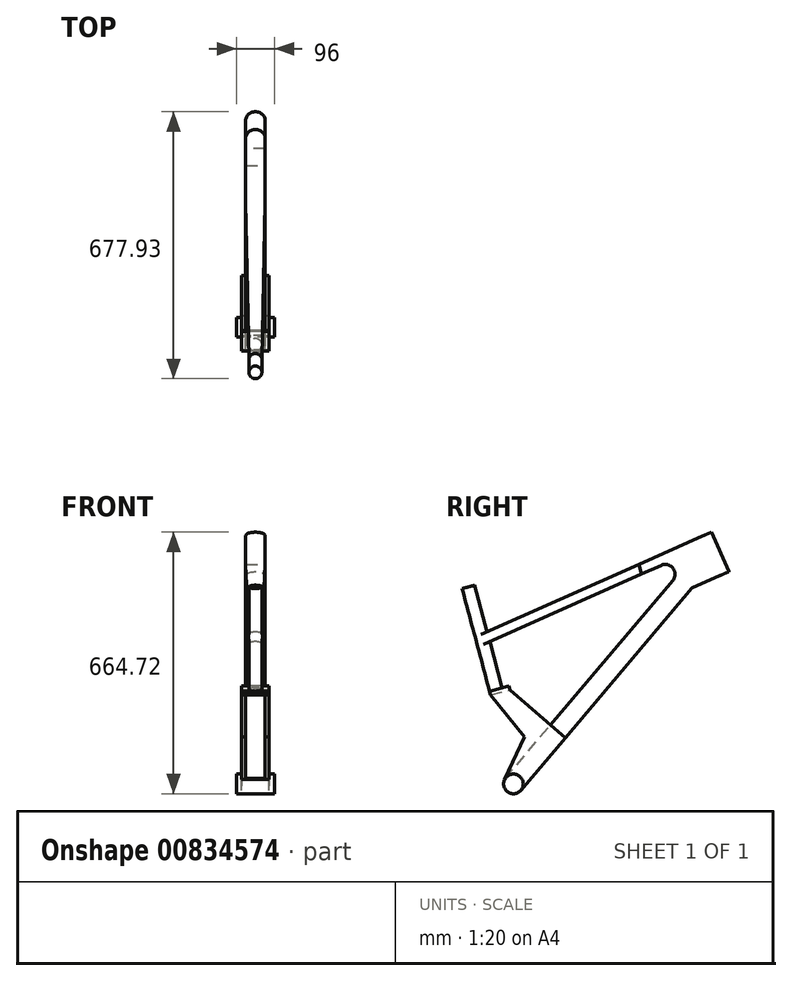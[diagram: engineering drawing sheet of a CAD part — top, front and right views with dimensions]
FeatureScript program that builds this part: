
annotation { "Feature Type Name" : "Feature", "Feature Type Description" : "" }
export const myFeature = defineFeature(function(context is Context, id is Id, definition is map)
    precondition{}
    {
        {
            var Q0;
            Q0=qCreatedBy(makeId("Right.planeOp"),FACE);
            var sketch = newSketch(context, id + "F0", { "sketchPlane" : qUnion([Q0])});
            skLineSegment(sketch, "E0", {"start": v(15, 17.71) * mm, "end": v(-114.4, 500.68) * mm});
            skCircle(sketch, "E1", {"center": v(0, 0) * mm, "radius": 25 * mm});
            skLineSegment(sketch, "E2", {"start": v(0, 0) * mm, "end": v(0, 629.55) * mm});
            skLineSegment(sketch, "E3", {"start": v(0, 629.55) * mm, "end": v(480, 629.55) * mm});
            skLineSegment(sketch, "E4", {"start": v(480, 629.55) * mm, "end": v(524.74, 529.06) * mm});
            skLineSegment(sketch, "E5", {"start": v(-148.94, 629.55) * mm, "end": v(480, 629.55) * mm});
            skLineSegment(sketch, "E6", {"start": v(0, 0) * mm, "end": v(991.3, 0) * mm});
            skLineSegment(sketch, "E7", {"start": v(524.74, 529.06) * mm, "end": v(571.33, 549.8) * mm});
            skLineSegment(sketch, "E8", {"start": v(571.33, 549.8) * mm, "end": v(802.76, 30) * mm});
            skCircle(sketch, "E9", {"center": v(802.76, 30) * mm, "radius": 368.5 * mm});
            skLineSegment(sketch, "E10", {"start": v(-560.19, -338.5) * mm, "end": v(1095.06, -338.5) * mm});
            skLineSegment(sketch, "E11", {"start": v(480, 629.55) * mm, "end": v(-81.9, 379.38) * mm});
            skCircle(sketch, "E12", {"center": v(-435, 30) * mm, "radius": 368.5 * mm});
            skLineSegment(sketch, "E13", {"start": v(0, 0) * mm, "end": v(498.3, 588.44) * mm});
            skLineSegment(sketch, "E14", {"start": v(0, 0) * mm, "end": v(-435, 0) * mm});
            skLineSegment(sketch, "E15", {"start": v(-114.4, 500.68) * mm, "end": v(-148.94, 629.55) * mm});
            skSolve(sketch);
        }
        {
            var Q0;
            Q0=qCreatedBy(makeId("Right.planeOp"),FACE);
            var sketch = newSketch(context, id + "F1", { "sketchPlane" : qUnion([Q0])});
            skLineSegment(sketch, "E16", {"start": v(480, 629.55) * mm, "end": v(502.84, 639.72) * mm});
            skLineSegment(sketch, "E17", {"start": v(524.74, 529.06) * mm, "end": v(547.58, 539.23) * mm});
            skLineSegment(sketch, "E18", {"start": v(480, 629.55) * mm, "end": v(524.74, 529.06) * mm});
            skLineSegment(sketch, "E19", {"start": v(502.84, 639.72) * mm, "end": v(547.58, 539.23) * mm});
            skSolve(sketch);
        }
        {
            var Q0;
            Q0=makeQuery(id+"F1.imprint","IMPRINT",FACE,{"disambiguationData":[TD([[makeQuery(id+"F1.imprint","IMPRINT",EDGE,{"derivedFrom":sQuery(id+"F1.wireOp",EDGE,"E16")}),-1.0]])]});
            var Q1;
            Q1=sQuery(id+"F1.wireOp",EDGE,"E18");
            revolve(context, id + "F2", {"surfaceOperationType" : NewSurfaceOperationType.NEW, "entities" : qUnion([Q0]), "axis" : qUnion([Q1]), "revolveType" : RevolveType.FULL, "oppositeDirection" : true});
        }
        {
            var Q0;
            Q0=sQuery(id+"F0.wireOp",EDGE,"E11");
            var Q1;
            Q1=sQuery(id+"F0.wireOp",VERTEX,"E3.end");
            cPlane(context, id + "F3", {"entities" : qUnion([Q0, Q1]), "cplaneType" : CPlaneType.LINE_POINT, "offset" : 25 * mm, "width" : 150 * mm, "height" : 150 * mm});
        }
        {
            var Q0;
            Q0=qCreatedBy(id+"F3.planeOp",FACE);
            var sketch = newSketch(context, id + "F4", { "sketchPlane" : qUnion([Q0])});
            skLineSegment(sketch, "E20.bottom", {"start": v(-25, 379.9) * mm, "end": v(25, 379.9) * mm});
            skLineSegment(sketch, "E20.top", {"start": v(-25, 354.9) * mm, "end": v(25, 354.9) * mm});
            skLineSegment(sketch, "E20.left", {"start": v(-25, 379.9) * mm, "end": v(-25, 354.9) * mm});
            skLineSegment(sketch, "E20.right", {"start": v(25, 379.9) * mm, "end": v(25, 354.9) * mm});
            skPoint(sketch, "E20.middle", {"position": v(0, 367.4) * mm});
            skPoint(sketch, "E21.visualSharp", {"position": v(25, 379.9) * mm});
            skPoint(sketch, "E22.visualSharp", {"position": v(25, 354.9) * mm});
            skPoint(sketch, "E23.visualSharp", {"position": v(-25, 354.9) * mm});
            skPoint(sketch, "E24.visualSharp", {"position": v(-25, 379.9) * mm});
            skSolve(sketch);
        }
        {
            var Q0;
            {var subQ0=sQuery(id+"F0.wireOp",EDGE,"E2");var subQ1=sQuery(id+"F0.wireOp",EDGE,"E1");var subQ2=makeQuery(id+"F0.imprint","INTERSECT",VERTEX,{"derivedFrom":[subQ1,subQ0]});Q0=makeQuery(id+"F0.imprint","IMPRINT",FACE,{"disambiguationData":[TD([[makeQuery(id+"F0.imprint","IMPRINT",EDGE,{"disambiguationData":[TD([[subQ2,-1.0]])],"derivedFrom":subQ1}),1.0]])]});}
            var Q1;
            {var subQ0=sQuery(id+"F0.wireOp",EDGE,"E1");var subQ1=sQuery(id+"F0.wireOp",EDGE,"E0");var subQ2=makeQuery(id+"F0.imprint","INTERSECT",VERTEX,{"derivedFrom":[subQ1,subQ0]});Q1=makeQuery(id+"F0.imprint","IMPRINT",FACE,{"disambiguationData":[TD([[makeQuery(id+"F0.imprint","IMPRINT",EDGE,{"disambiguationData":[TD([[subQ2,1.0]])],"derivedFrom":subQ1}),1.0]])]});}
            var Q2;
            {var subQ0=sQuery(id+"F0.wireOp",EDGE,"E1");var subQ1=sQuery(id+"F0.wireOp",EDGE,"E0");var subQ2=makeQuery(id+"F0.imprint","INTERSECT",VERTEX,{"derivedFrom":[subQ1,subQ0]});Q2=makeQuery(id+"F0.imprint","IMPRINT",FACE,{"disambiguationData":[TD([[makeQuery(id+"F0.imprint","IMPRINT",EDGE,{"disambiguationData":[TD([[subQ2,1.0]])],"derivedFrom":subQ1}),-1.0]])]});}
            var Q3;
            {var subQ0=sQuery(id+"F0.wireOp",EDGE,"E6");var subQ1=sQuery(id+"F0.wireOp",EDGE,"E1");var subQ2=makeQuery(id+"F0.imprint","INTERSECT",VERTEX,{"derivedFrom":[subQ1,subQ0]});Q3=makeQuery(id+"F0.imprint","IMPRINT",FACE,{"disambiguationData":[TD([[makeQuery(id+"F0.imprint","IMPRINT",EDGE,{"disambiguationData":[TD([[subQ2,-1.0]])],"derivedFrom":subQ1}),1.0]])]});}
            var Q4;
            {var subQ0=sQuery(id+"F0.wireOp",EDGE,"E6");var subQ1=sQuery(id+"F0.wireOp",EDGE,"E1");var subQ2=makeQuery(id+"F0.imprint","INTERSECT",VERTEX,{"derivedFrom":[subQ1,subQ0]});Q4=makeQuery(id+"F0.imprint","IMPRINT",FACE,{"disambiguationData":[TD([[makeQuery(id+"F0.imprint","IMPRINT",EDGE,{"disambiguationData":[TD([[subQ2,1.0]])],"derivedFrom":subQ1}),1.0]])]});}
            extrude(context, id + "F5", {"entities" : qUnion([Q0, Q1, Q2, Q3, Q4]), "endBound" : BoundingType.SYMMETRIC, "depth" : 96 * mm, "offsetDistance" : 25 * mm});
        }
        {
            var Q0;
            Q0=sQuery(id+"F0.wireOp",EDGE,"E13");
            var Q1;
            Q1=sQuery(id+"F0.wireOp",VERTEX,"E2.start");
            cPlane(context, id + "F6", {"entities" : qUnion([Q0, Q1]), "cplaneType" : CPlaneType.LINE_POINT, "offset" : 25 * mm, "width" : 150 * mm, "height" : 150 * mm});
        }
        {
            var Q0;
            Q0=qCreatedBy(id+"F6.planeOp",FACE);
            var sketch = newSketch(context, id + "F7", { "sketchPlane" : qUnion([Q0])});
            skLineSegment(sketch, "E25.bottom", {"start": v(25, -25) * mm, "end": v(-25, -25) * mm});
            skLineSegment(sketch, "E25.top", {"start": v(25, 25) * mm, "end": v(-25, 25) * mm});
            skPoint(sketch, "E25.middle", {"position": v(0, 0) * mm});
            skLineSegment(sketch, "E26", {"start": v(25, -25) * mm, "end": v(25, 25) * mm});
            skLineSegment(sketch, "E27", {"start": v(-25, -25) * mm, "end": v(-25, 25) * mm});
            skSolve(sketch);
        }
        {
            var Q0;
            Q0 = qSketchRegion(id + "F7", true);
            var Q1;
            Q1=makeQuery(id+"F2.opRevolve","SWEPT_FACE",FACE,{"disambiguationData":[OSD([sQuery(id+"F1.wireOp",EDGE,"E19")])]});
            extrude(context, id + "F8", {"entities" : qUnion([Q0]), "operationType" : NewBodyOperationType.ADD, "endBound" : BoundingType.UP_TO_SURFACE, "depth" : 25 * mm, "endBoundEntityFace" : qUnion([Q1]), "offsetDistance" : 25 * mm});
        }
        {
            var Q0;
            Q0=sQuery(id+"F0.wireOp",VERTEX,"E0.end");
            var Q1;
            Q1=sQuery(id+"F0.wireOp",EDGE,"E0");
            cPlane(context, id + "F9", {"entities" : qUnion([Q0, Q1]), "cplaneType" : CPlaneType.LINE_POINT, "offset" : 25 * mm, "width" : 150 * mm, "height" : 150 * mm});
        }
        {
            var Q0;
            Q0=qCreatedBy(id+"F9.planeOp",FACE);
            var sketch = newSketch(context, id + "F10", { "sketchPlane" : qUnion([Q0])});
            skCircle(sketch, "E28", {"center": v(0, 19.07) * mm, "radius": 16.5 * mm});
            skSolve(sketch);
        }
        {
            var Q0;
            Q0 = qSketchRegion(id + "F10", true);
            extrude(context, id + "F11", {"entities" : qUnion([Q0]), "oppositeDirection" : true, "depth" : 280 * mm, "offsetDistance" : 25 * mm});
        }
        {
            var Q0;
            Q0 = qSketchRegion(id + "F4", true);
            extrude(context, id + "F12", {"entities" : qUnion([Q0]), "operationType" : NewBodyOperationType.ADD, "depth" : 621 * mm, "offsetDistance" : 25 * mm});
        }
        {
            var Q0;
            Q0=makeQuery(id+"F12.boolean.opBoolean","MERGE",FACE,{"derivedFrom":[makeQuery(id+"F8.opExtrude","SWEPT_FACE",FACE,{"disambiguationData":[OSD([sQuery(id+"F7.wireOp",EDGE,"E26")])]}),makeQuery(id+"F12.opExtrude","SWEPT_FACE",FACE,{"disambiguationData":[OSD([sQuery(id+"F4.wireOp",EDGE,"E20.right")])]})]});
            var sketch = newSketch(context, id + "F13", { "sketchPlane" : qUnion([Q0])});
            skLineSegment(sketch, "E29", {"start": v(480, 629.55) * mm, "end": v(524.74, 529.06) * mm});
            skLineSegment(sketch, "E30", {"start": v(524.74, 529.06) * mm, "end": v(349, 450.82) * mm});
            skLineSegment(sketch, "E31", {"start": v(454.17, 497.64) * mm, "end": v(509.6, 563.09) * mm});
            skLineSegment(sketch, "E32", {"start": v(480, 629.55) * mm, "end": v(349, 571.23) * mm});
            skLineSegment(sketch, "E33", {"start": v(349, 571.23) * mm, "end": v(349, 450.82) * mm});
            skSolve(sketch);
        }
        {
            var Q0;
            Q0 = qSketchRegion(id + "F13", true);
            var Q1;
            Q1=makeQuery(id+"F12.boolean.opBoolean","MERGE",FACE,{"derivedFrom":[makeQuery(id+"F8.opExtrude","SWEPT_FACE",FACE,{"disambiguationData":[OSD([sQuery(id+"F7.wireOp",EDGE,"E27")])]}),makeQuery(id+"F12.opExtrude","SWEPT_FACE",FACE,{"disambiguationData":[OSD([sQuery(id+"F4.wireOp",EDGE,"E20.left")])]})]});
            extrude(context, id + "F14", {"entities" : qUnion([Q0]), "operationType" : NewBodyOperationType.ADD, "endBound" : BoundingType.UP_TO_SURFACE, "oppositeDirection" : true, "depth" : 25 * mm, "endBoundEntityFace" : qUnion([Q1]), "offsetDistance" : 25 * mm});
        }
        {
            var Q0;
            Q0=makeQuery(id+"F14.boolean.opBoolean","MERGE",FACE,{"derivedFrom":[makeQuery(id+"F12.boolean.opBoolean","MERGE",FACE,{"derivedFrom":[makeQuery(id+"F8.opExtrude","SWEPT_FACE",FACE,{"disambiguationData":[OSD([sQuery(id+"F7.wireOp",EDGE,"E26")])]}),makeQuery(id+"F12.opExtrude","SWEPT_FACE",FACE,{"disambiguationData":[OSD([sQuery(id+"F4.wireOp",EDGE,"E20.right")])]})]}),makeQuery(id+"F14.opExtrude","CAP_FACE",FACE,{"disambiguationData":[OSD([sQuery(id+"F13.wireOp",EDGE,"E29"),sQuery(id+"F13.wireOp",EDGE,"E30"),sQuery(id+"F13.wireOp",EDGE,"E32"),sQuery(id+"F13.wireOp",EDGE,"E33")])],"isStart":true})]});
            var sketch = newSketch(context, id + "F15", { "sketchPlane" : qUnion([Q0])});
            skLineSegment(sketch, "E34", {"start": v(349, 543.86) * mm, "end": v(375.52, 555.67) * mm});
            skLineSegment(sketch, "E35", {"start": v(349, 450.82) * mm, "end": v(404.77, 516.68) * mm});
            skArc(sketch, "E36", {"start": v(404.77, 516.68) * mm, "mid": v(405.7, 547.83) * mm, "end": v(375.52, 555.67) * mm});
            skLineSegment(sketch, "E37", {"start": v(349, 543.86) * mm, "end": v(349, 450.82) * mm});
            skSolve(sketch);
        }
        {
            var Q0;
            Q0 = qSketchRegion(id + "F15", true);
            extrude(context, id + "F16", {"entities" : qUnion([Q0]), "operationType" : NewBodyOperationType.REMOVE, "endBound" : BoundingType.UP_TO_NEXT, "oppositeDirection" : true, "depth" : 25 * mm, "offsetDistance" : 25 * mm});
        }
        {
            var Q0;
            Q0=qCreatedBy(makeId("Right.planeOp"),FACE);
            var sketch = newSketch(context, id + "F17", { "sketchPlane" : qUnion([Q0])});
            skCircle(sketch, "E38", {"center": v(90, 110) * mm, "radius": 20 * mm});
            skLineSegment(sketch, "E39", {"start": v(106.49, 121.32) * mm, "end": v(81, 158.46) * mm});
            skLineSegment(sketch, "E40", {"start": v(0, 181.87) * mm, "end": v(-420.23, 77.94) * mm});
            skLineSegment(sketch, "E41", {"start": v(-420.23, 77.94) * mm, "end": v(-457.48, 18.01) * mm});
            skLineSegment(sketch, "E42", {"start": v(-457.48, 18.01) * mm, "end": v(-415.8, 18.01) * mm});
            skLineSegment(sketch, "E43", {"start": v(-415.8, 18.01) * mm, "end": v(-393.05, 48.75) * mm});
            skLineSegment(sketch, "E44", {"start": v(0, 121.22) * mm, "end": v(83.21, 91.19) * mm});
            skLineSegment(sketch, "E45", {"start": v(-393.05, 48.75) * mm, "end": v(0, 121.22) * mm});
            skPoint(sketch, "E46.orphan", {"position": v(49.08, 119.9) * mm});
            skLineSegment(sketch, "E47", {"start": v(0, 181.87) * mm, "end": v(81, 158.46) * mm});
            skPoint(sketch, "E48.orphan", {"position": v(55.5, 195.6) * mm});
            skSolve(sketch);
        }
        {
            var Q0;
            Q0=qCreatedBy(makeId("Right.planeOp"),FACE);
            var sketch = newSketch(context, id + "F18", { "sketchPlane" : qUnion([Q0])});
            skCircle(sketch, "E49", {"center": v(0, 0) * mm, "radius": 25 * mm});
            skLineSegment(sketch, "E50", {"start": v(-22.3, 11.3) * mm, "end": v(58.11, 181.73) * mm});
            skLineSegment(sketch, "E51", {"start": v(58.11, 181.73) * mm, "end": v(132.17, 117.4) * mm});
            skLineSegment(sketch, "E52", {"start": v(132.17, 117.4) * mm, "end": v(19.08, -16.16) * mm});
            skLineSegment(sketch, "E53", {"start": v(-57.88, 225.95) * mm, "end": v(-8.13, 239.28) * mm});
            skLineSegment(sketch, "E54", {"start": v(-8.13, 239.28) * mm, "end": v(58.11, 181.73) * mm});
            skLineSegment(sketch, "E55", {"start": v(-57.88, 225.95) * mm, "end": v(28.61, 119.21) * mm});
            skSolve(sketch);
        }
        {
            var Q0;
            Q0 = qSketchRegion(id + "F18", true);
            extrude(context, id + "F19", {"entities" : qUnion([Q0]), "endBound" : BoundingType.SYMMETRIC, "depth" : 70 * mm, "offsetDistance" : 25 * mm});
        }
        {
            var Q0;
            Q0=makeQuery(id+"F16.boolean.opBoolean","MERGE",FACE,{"derivedFrom":[makeQuery(id+"F8.opExtrude","SWEPT_FACE",FACE,{"disambiguationData":[OSD([sQuery(id+"F7.wireOp",EDGE,"E25.bottom")])]})],"fromTools":[makeQuery(id+"F16.opExtrude","SWEPT_FACE",FACE,{"disambiguationData":[OSD([sQuery(id+"F15.wireOp",EDGE,"E35")])]})]});
            var sketch = newSketch(context, id + "F20", { "sketchPlane" : qUnion([Q0])});
            skLineSegment(sketch, "E56.bottom", {"start": v(-25, -25) * mm, "end": v(25, -25) * mm});
            skLineSegment(sketch, "E56.top", {"start": v(-25, 225) * mm, "end": v(25, 225) * mm});
            skLineSegment(sketch, "E56.left", {"start": v(-25, -25) * mm, "end": v(-25, 225) * mm});
            skLineSegment(sketch, "E56.right", {"start": v(25, -25) * mm, "end": v(25, 225) * mm});
            skSolve(sketch);
        }
        {
            var Q0;
            Q0 = qSketchRegion(id + "F20", true);
            var Q1;
            Q1=makeQuery(id+"F19.opExtrude","SWEPT_FACE",FACE,{"disambiguationData":[OSD([sQuery(id+"F18.wireOp",EDGE,"E53")])]});
            extrude(context, id + "F21", {"entities" : qUnion([Q0]), "operationType" : NewBodyOperationType.REMOVE, "endBound" : BoundingType.UP_TO_SURFACE, "depth" : 146 * mm, "endBoundEntityFace" : qUnion([Q1]), "offsetDistance" : 25 * mm});
        }
        {
            var Q0;
            Q0=makeQuery(id+"F19.opExtrude","SWEPT_FACE",FACE,{"disambiguationData":[OSD([sQuery(id+"F18.wireOp",EDGE,"E53")])]});
            var sketch = newSketch(context, id + "F22", { "sketchPlane" : qUnion([Q0])});
            skLineSegment(sketch, "E57.bottom", {"start": v(35, 2.57) * mm, "end": v(-35, 2.57) * mm});
            skLineSegment(sketch, "E57.top", {"start": v(35, 54.07) * mm, "end": v(-35, 54.07) * mm});
            skLineSegment(sketch, "E57.left", {"start": v(35, 2.57) * mm, "end": v(35, 54.07) * mm});
            skLineSegment(sketch, "E57.right", {"start": v(-35, 2.57) * mm, "end": v(-35, 54.07) * mm});
            skSolve(sketch);
        }
        {
            var Q0;
            Q0=makeQuery(id+"F11.opExtrude","CAP_FACE",FACE,{"disambiguationData":[OSD([sQuery(id+"F10.wireOp",EDGE,"E28")])],"isStart":true});
            var sketch = newSketch(context, id + "F23", { "sketchPlane" : qUnion([Q0])});
            skCircle(sketch, "E58", {"center": v(0, 19.07) * mm, "radius": 16.5 * mm});
            skLineSegment(sketch, "E59", {"start": v(-16.5, 18.75) * mm, "end": v(-25, 451.95) * mm});
            skLineSegment(sketch, "E60", {"start": v(16.5, 18.75) * mm, "end": v(25, 451.95) * mm});
            skLineSegment(sketch, "E61", {"start": v(25, 451.95) * mm, "end": v(-25, 451.95) * mm});
            skLineSegment(sketch, "E62", {"start": v(0, 2.57) * mm, "end": v(-58.1, 2.57) * mm});
            skLineSegment(sketch, "E63", {"start": v(-58.1, 2.57) * mm, "end": v(-58.1, 452.6) * mm});
            skLineSegment(sketch, "E64", {"start": v(-58.1, 452.6) * mm, "end": v(-25, 451.95) * mm});
            skLineSegment(sketch, "E65", {"start": v(25, 451.95) * mm, "end": v(64.52, 451.17) * mm});
            skLineSegment(sketch, "E66", {"start": v(64.52, 451.17) * mm, "end": v(64.52, 2.57) * mm});
            skLineSegment(sketch, "E67", {"start": v(64.52, 2.57) * mm, "end": v(0, 2.57) * mm});
            skLineSegment(sketch, "E68", {"start": v(-58.1, 121.2) * mm, "end": v(64.52, 118.8) * mm});
            skSolve(sketch);
        }
        {
            var Q0;
            {var subQ1=sQuery(id+"F23.wireOp",EDGE,"E62");Q0=makeQuery(id+"F23.imprint","IMPRINT",FACE,{"disambiguationData":[TD([[makeQuery(id+"F23.imprint","IMPRINT",EDGE,{"derivedFrom":subQ1}),-1.0]])]});}
            var Q1;
            {var subQ0=sQuery(id+"F23.wireOp",EDGE,"E64");Q1=makeQuery(id+"F23.imprint","IMPRINT",FACE,{"disambiguationData":[TD([[makeQuery(id+"F23.imprint","IMPRINT",EDGE,{"derivedFrom":subQ0}),-1.0]])]});}
            var Q2;
            {var subQ0=sQuery(id+"F23.wireOp",EDGE,"E67");Q2=makeQuery(id+"F23.imprint","IMPRINT",FACE,{"disambiguationData":[TD([[makeQuery(id+"F23.imprint","IMPRINT",EDGE,{"derivedFrom":subQ0}),-1.0]])]});}
            var Q3;
            {var subQ0=sQuery(id+"F23.wireOp",EDGE,"E65");Q3=makeQuery(id+"F23.imprint","IMPRINT",FACE,{"disambiguationData":[TD([[makeQuery(id+"F23.imprint","IMPRINT",EDGE,{"derivedFrom":subQ0}),-1.0]])]});}
            extrude(context, id + "F24", {"entities" : qUnion([Q0, Q1, Q2, Q3]), "operationType" : NewBodyOperationType.REMOVE, "oppositeDirection" : true, "depth" : 142 * mm, "offsetDistance" : 25 * mm});
        }
        {
            var Q0;
            {var subQ0=sQuery(id+"F23.wireOp",EDGE,"E67");Q0=makeQuery(id+"F23.imprint","IMPRINT",FACE,{"disambiguationData":[TD([[makeQuery(id+"F23.imprint","IMPRINT",EDGE,{"derivedFrom":subQ0}),-1.0]])]});}
            var Q1;
            {var subQ1=sQuery(id+"F23.wireOp",EDGE,"E62");Q1=makeQuery(id+"F23.imprint","IMPRINT",FACE,{"disambiguationData":[TD([[makeQuery(id+"F23.imprint","IMPRINT",EDGE,{"derivedFrom":subQ1}),-1.0]])]});}
            var Q2;
            Q2=makeQuery(id+"FmZW0NIcieUc2Zm_3.boolean.opBoolean","MERGE",FACE,{"derivedFrom":[makeQuery(id+"F11.opExtrude","CAP_FACE",FACE,{"disambiguationData":[OSD([sQuery(id+"F10.wireOp",EDGE,"E28")])],"isStart":false}),makeQuery(id+"FmZW0NIcieUc2Zm_3.opExtrude","CAP_FACE",FACE,{"disambiguationData":[OSD([sQuery(id+"F22.wireOp",EDGE,"E57.bottom"),sQuery(id+"F22.wireOp",EDGE,"E57.top"),sQuery(id+"F22.wireOp",EDGE,"E57.left"),sQuery(id+"F22.wireOp",EDGE,"E57.right")])],"isStart":true})]});
            var Q3;
            Q3=makeQuery(id+"FmZW0NIcieUc2Zm_3.boolean.opBoolean","MERGE",VERTEX,{"derivedFrom":[makeQuery(id+"F19.opExtrude","CAP_VERTEX",VERTEX,{"disambiguationData":[OSD([sQuery(id+"F18.wireOp",EDGE,"E53"),sQuery(id+"F18.wireOp",EDGE,"E54")])],"isStart":false}),makeQuery(id+"FmZW0NIcieUc2Zm_3.opExtrude","CAP_VERTEX",VERTEX,{"disambiguationData":[OSD([sQuery(id+"F22.wireOp",EDGE,"E57.top"),sQuery(id+"F22.wireOp",EDGE,"E57.left")])],"isStart":true})]});
            extrude(context, id + "F25", {"entities" : qUnion([Q0, Q1]), "operationType" : NewBodyOperationType.REMOVE, "endBound" : BoundingType.UP_TO_SURFACE, "oppositeDirection" : true, "depth" : 300 * mm, "endBoundEntityFace" : qUnion([Q2]), "endBoundEntityVertex" : qUnion([Q3]), "offsetDistance" : 25 * mm});
        }
        {
            var Q0;
            {var subQ1=makeQuery(id+"F21.boolean.opBoolean","COPY",EDGE,{"derivedFrom":makeQuery(id+"F21.opExtrude","CAP_EDGE",EDGE,{"disambiguationData":[OSD([sQuery(id+"F20.wireOp",EDGE,"E56.left")])],"isStart":false})});Q0=makeQuery(id+"F22.imprint","IMPRINT",FACE,{"disambiguationData":[TD([[makeQuery(id+"F22.imprint","IMPRINT",EDGE,{"derivedFrom":subQ1}),-1.0]])]});}
            var Q1;
            {var subQ0=sQuery(id+"F22.wireOp",EDGE,"E57.left");Q1=makeQuery(id+"F22.imprint","IMPRINT",FACE,{"disambiguationData":[TD([[makeQuery(id+"F22.imprint","IMPRINT",EDGE,{"derivedFrom":subQ0}),1.0]])]});}
            var Q2;
            {var subQ0=sQuery(id+"F22.wireOp",EDGE,"E57.right");Q2=makeQuery(id+"F22.imprint","IMPRINT",FACE,{"disambiguationData":[TD([[makeQuery(id+"F22.imprint","IMPRINT",EDGE,{"derivedFrom":subQ0}),-1.0]])]});}
            extrude(context, id + "F26", {"entities" : qUnion([Q0, Q1, Q2]), "operationType" : NewBodyOperationType.ADD, "depth" : 10 * mm, "offsetDistance" : 25 * mm});
        }
    });
